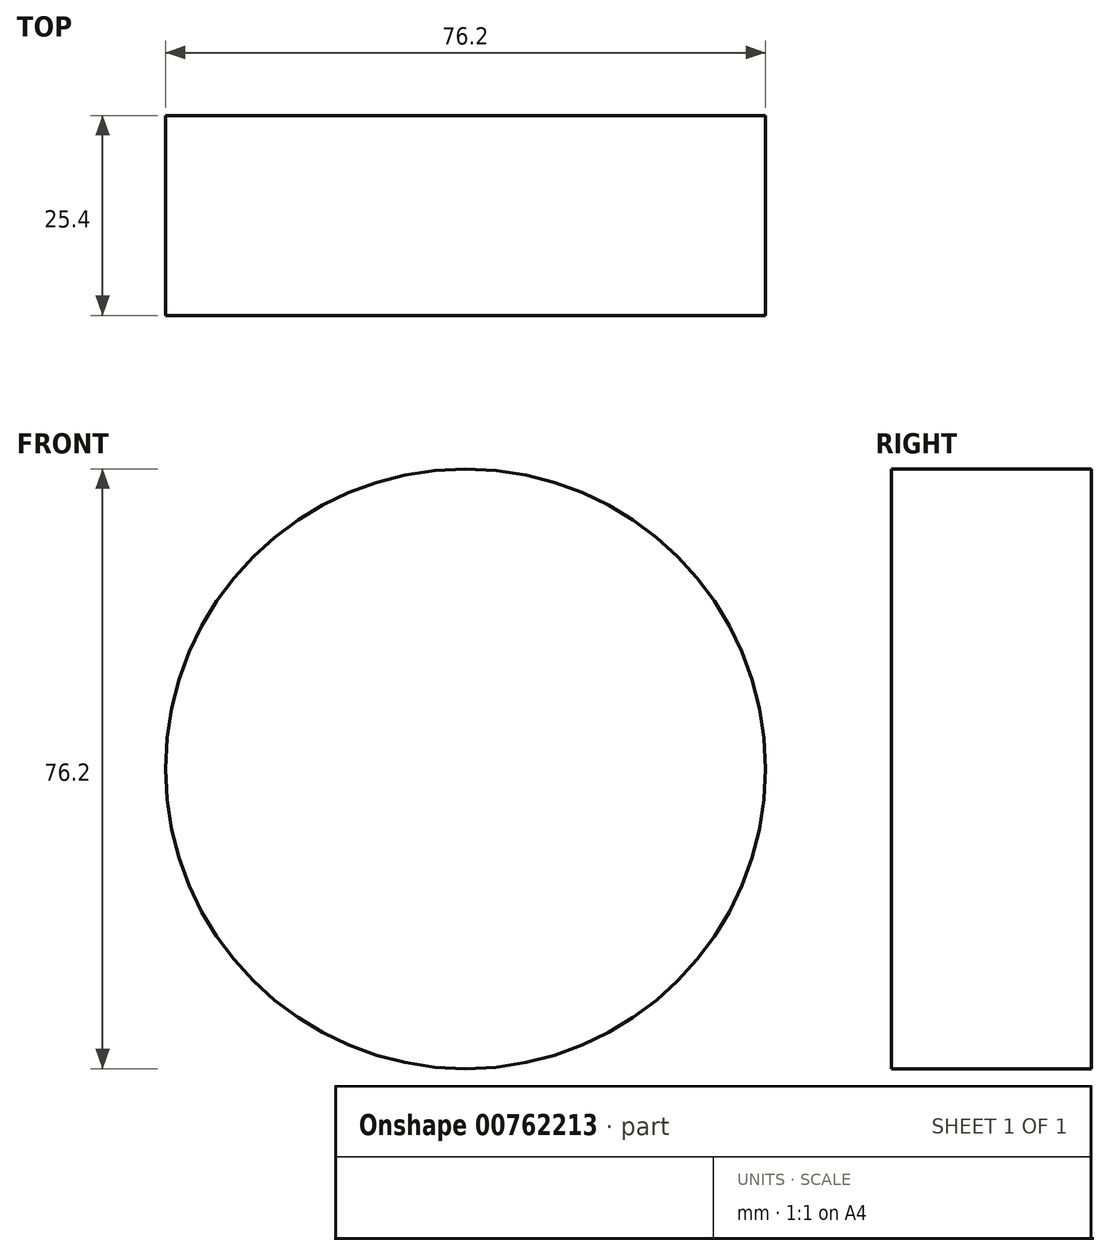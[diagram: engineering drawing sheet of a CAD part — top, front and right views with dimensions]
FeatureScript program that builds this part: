
annotation { "Feature Type Name" : "Feature", "Feature Type Description" : "" }
export const myFeature = defineFeature(function(context is Context, id is Id, definition is map)
    precondition{}
    {
        {
            var Q0;
            Q0=qCreatedBy(makeId("Front.planeOp"),FACE);
            var sketch = newSketch(context, id + "F0", { "sketchPlane" : qUnion([Q0])});
            skCircle(sketch, "E0", {"center": v(0, 0) * mm, "radius": 38.1 * mm});
            skSolve(sketch);
        }
        {
            var Q0;
            Q0=makeQuery(id+"F0.imprint","IMPRINT",FACE,{"disambiguationData":[TD([[makeQuery(id+"F0.imprint","IMPRINT",EDGE,{"derivedFrom":sQuery(id+"F0.wireOp",EDGE,"E0")}),1.0]])]});
            var Q1;
            Q1=sQuery(id+"F0.wireOp",EDGE,"E0");
            extrude(context, id + "F1", {"entities" : qUnion([Q0]), "surfaceOperationType" : NewSurfaceOperationType.ADD, "surfaceEntities" : qUnion([Q1]), "depth" : 25.4 * mm, "offsetDistance" : 25.4 * mm});
        }
    });
